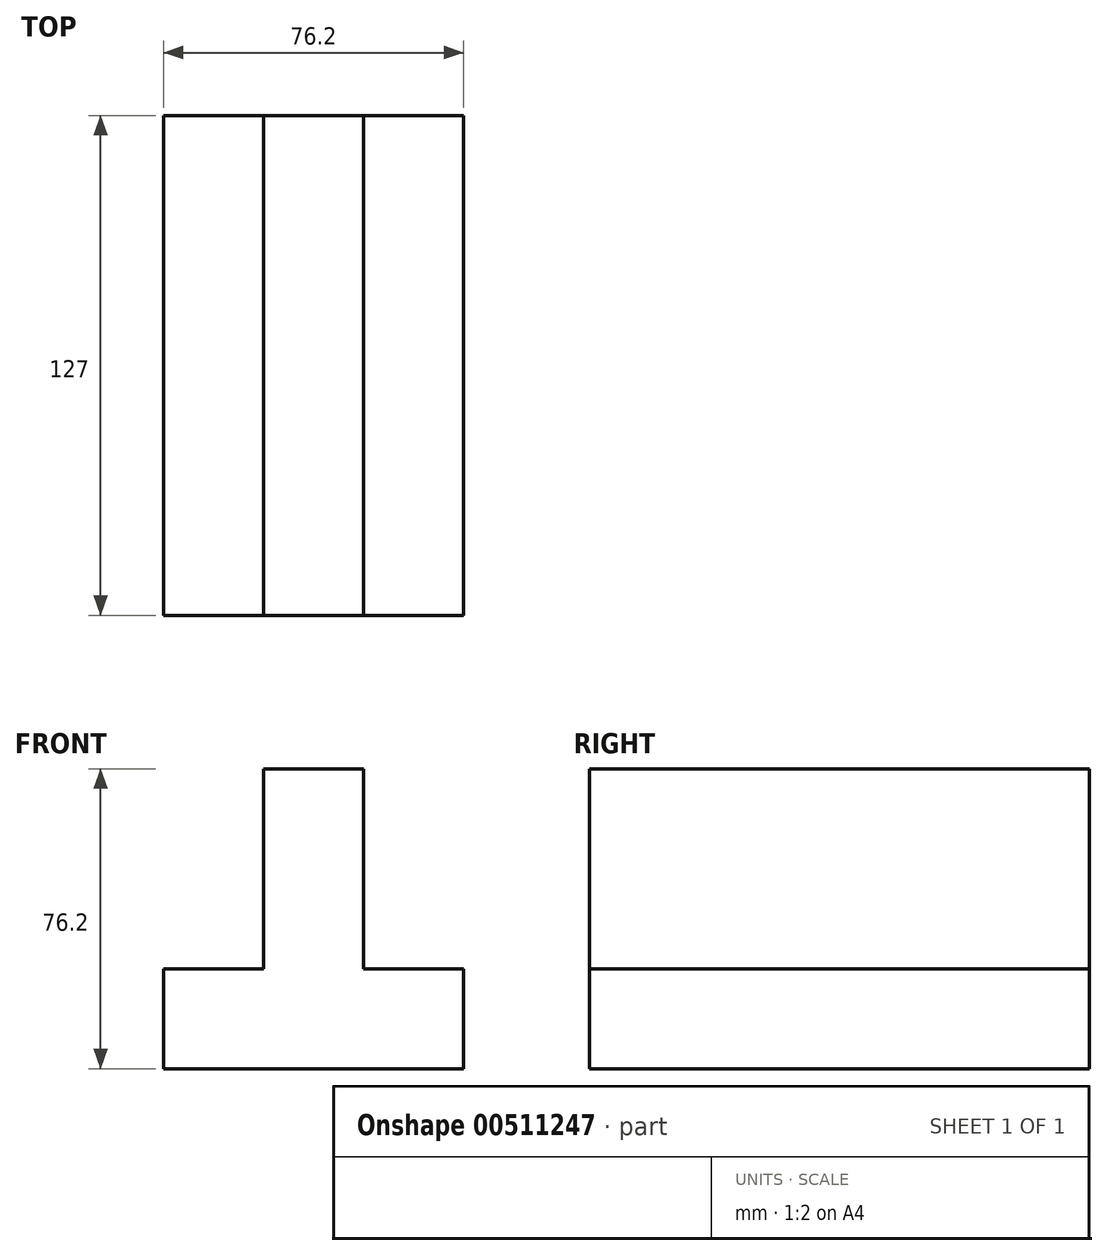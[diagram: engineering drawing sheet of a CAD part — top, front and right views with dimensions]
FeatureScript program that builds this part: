
annotation { "Feature Type Name" : "Feature", "Feature Type Description" : "" }
export const myFeature = defineFeature(function(context is Context, id is Id, definition is map)
    precondition{}
    {
        {
            var Q0;
            Q0=qCreatedBy(makeId("Front.planeOp"),FACE);
            var sketch = newSketch(context, id + "F0", { "sketchPlane" : qUnion([Q0])});
            skLineSegment(sketch, "E0", {"start": v(-35.44, -27.4) * mm, "end": v(40.76, -27.4) * mm});
            skLineSegment(sketch, "E1", {"start": v(40.76, -27.4) * mm, "end": v(40.76, -2) * mm});
            skLineSegment(sketch, "E2", {"start": v(40.76, -2) * mm, "end": v(15.36, -2) * mm});
            skLineSegment(sketch, "E3", {"start": v(15.36, -2) * mm, "end": v(15.36, 48.8) * mm});
            skLineSegment(sketch, "E4", {"start": v(15.36, 48.8) * mm, "end": v(-10.04, 48.8) * mm});
            skLineSegment(sketch, "E5", {"start": v(-10.04, 48.8) * mm, "end": v(-10.04, -2) * mm});
            skLineSegment(sketch, "E6", {"start": v(-10.04, -2) * mm, "end": v(-35.44, -2) * mm});
            skLineSegment(sketch, "E7", {"start": v(-35.44, -2) * mm, "end": v(-35.44, -27.4) * mm});
            skSolve(sketch);
        }
        {
            var Q0;
            Q0 = qSketchRegion(id + "F0", true);
            extrude(context, id + "F1", {"entities" : qUnion([Q0]), "depth" : 127 * mm});
        }
    });
